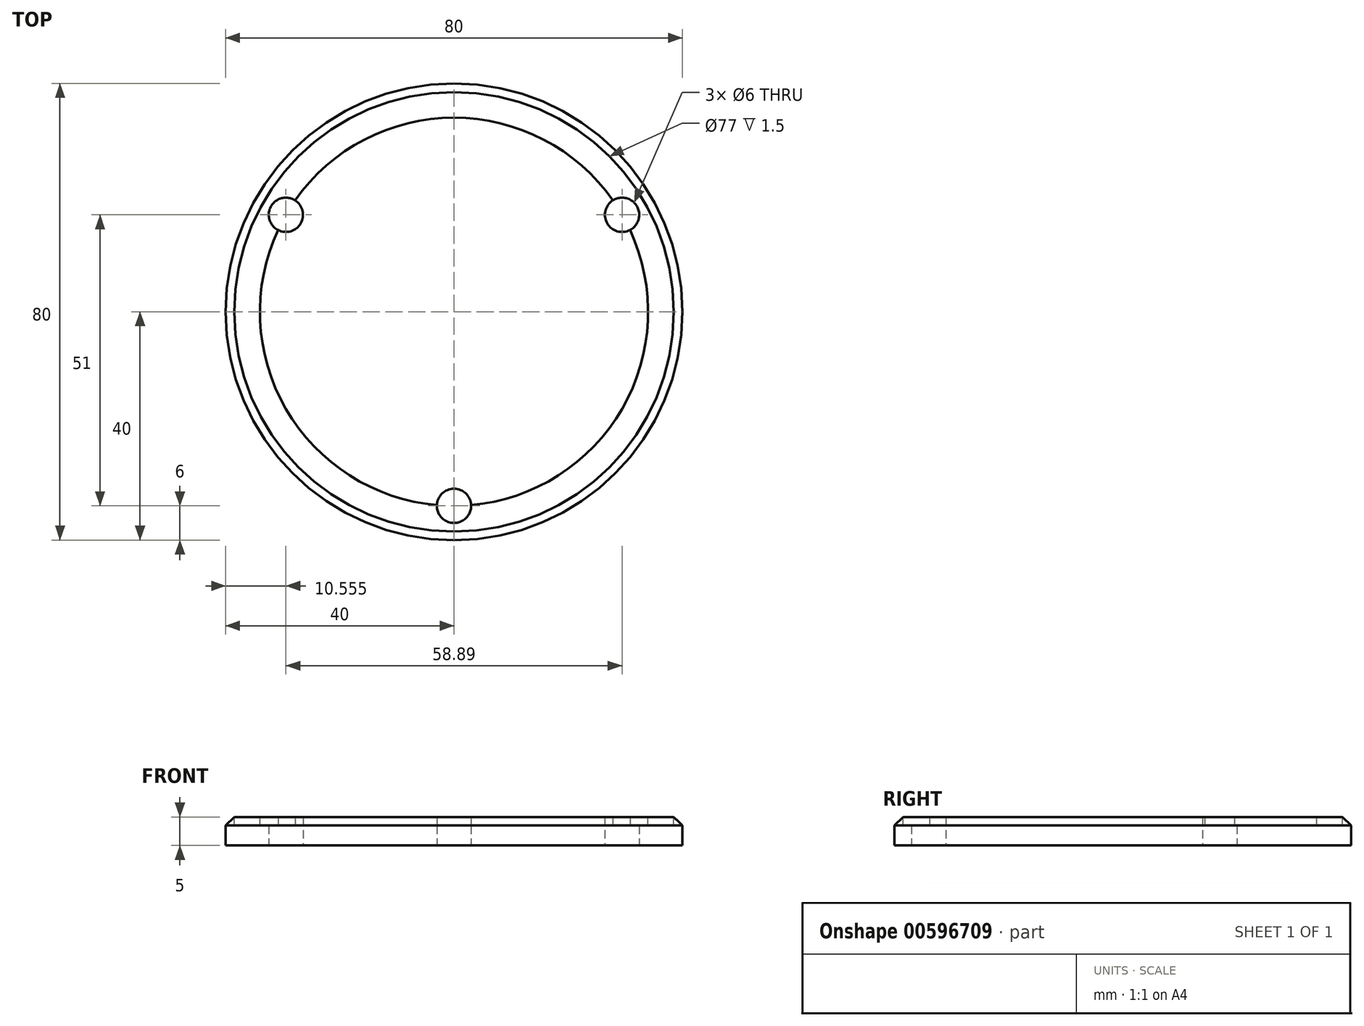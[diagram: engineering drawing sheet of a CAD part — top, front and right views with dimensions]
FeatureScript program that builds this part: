
annotation { "Feature Type Name" : "Feature", "Feature Type Description" : "" }
export const myFeature = defineFeature(function(context is Context, id is Id, definition is map)
    precondition{}
    {
        {
            var Q0;
            Q0=qCreatedBy(makeId("Top.planeOp"),FACE);
            var sketch = newSketch(context, id + "F0", { "sketchPlane" : qUnion([Q0])});
            skCircle(sketch, "E0", {"center": v(0, 0) * mm, "radius": 40 * mm});
            skSolve(sketch);
        }
        {
            var Q0;
            Q0 = qSketchRegion(id + "F0", true);
            extrude(context, id + "F1", {"entities" : qUnion([Q0]), "depth" : 5 * mm, "offsetDistance" : 25 * mm});
        }
        {
            var Q0;
            Q0=makeQuery(id+"F1.opExtrude","CAP_EDGE",EDGE,{"disambiguationData":[OSD([sQuery(id+"F0.wireOp",EDGE,"E0")])],"isStart":false});
            chamfer(context, id + "F2", {"entities" : qUnion([Q0]), "width" : 1.5 * mm, "tangentPropagation" : true});
        }
        {
            var Q0;
            Q0=makeQuery(id+"F1.opExtrude","CAP_FACE",FACE,{"disambiguationData":[OSD([sQuery(id+"F0.wireOp",EDGE,"E0")])],"isStart":false});
            var sketch = newSketch(context, id + "F3", { "sketchPlane" : qUnion([Q0])});
            skCircle(sketch, "E1", {"center": v(0, 0) * mm, "radius": 34 * mm});
            skSolve(sketch);
        }
        {
            var Q0;
            Q0=makeQuery(id+"F3.imprint","IMPRINT",FACE,{"disambiguationData":[TD([[makeQuery(id+"F3.imprint","IMPRINT",EDGE,{"derivedFrom":sQuery(id+"F3.wireOp",EDGE,"E1")}),-1.0]])]});
            extrude(context, id + "F4", {"entities" : qUnion([Q0]), "operationType" : NewBodyOperationType.REMOVE, "oppositeDirection" : true, "depth" : 1.5 * mm, "offsetDistance" : 25 * mm});
        }
        {
            var Q0;
            Q0=makeQuery(id+"F1.opExtrude","CAP_FACE",FACE,{"disambiguationData":[OSD([sQuery(id+"F0.wireOp",EDGE,"E0")])],"isStart":false});
            var sketch = newSketch(context, id + "F5", { "sketchPlane" : qUnion([Q0])});
            skCircle(sketch, "E2", {"center": v(0, -34) * mm, "radius": 3 * mm});
            skCircle(sketch, "E3.1.0", {"center": v(29.44, 17) * mm, "radius": 3 * mm});
            skCircle(sketch, "E3.2.0", {"center": v(-29.44, 17) * mm, "radius": 3 * mm});
            skPoint(sketch, "E3.center", {"position": v(0, 0) * mm});
            skSolve(sketch);
        }
        {
            var Q0;
            Q0=sQuery(id+"F5.wireOp",VERTEX,"E3.1.0.center");
            var Q1;
            Q1=sQuery(id+"F5.wireOp",VERTEX,"E2.center");
            var Q2;
            Q2=sQuery(id+"F5.wireOp",VERTEX,"E3.2.0.center");
            var Q3;
            Q3=makeQuery(id+"F1.opExtrude","SWEPT_BODY",BODY,{"disambiguationData":[OSD([sQuery(id+"F0.wireOp",EDGE,"E0")])]});
            hole(context, id + "F6", {"style" : HoleStyle.SIMPLE, "endStyle" : HoleEndStyle.BLIND, "holeDiameter" : 6 * mm, "majorDiameter" : 5 * mm, "holeDepth" : 10 * mm, "isTappedThrough" : true, "tappedDepth" : 12 * mm, "tapClearance" : 3, "startFromSketch" : true, "locations" : qUnion([Q0, Q1, Q2]), "scope" : qUnion([Q3])});
        }
    });
